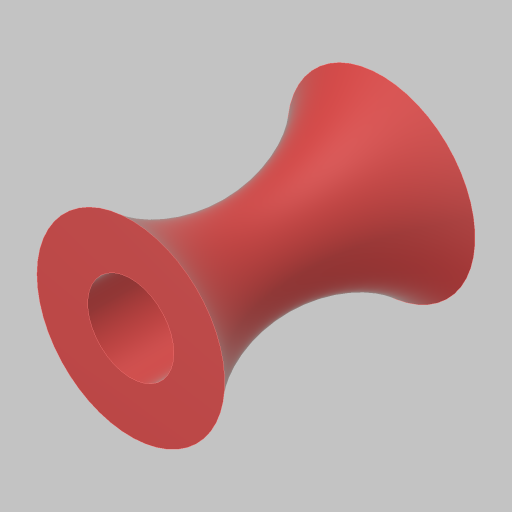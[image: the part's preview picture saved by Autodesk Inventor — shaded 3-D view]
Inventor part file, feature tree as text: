
AUTODESK INVENTOR PART (.ipt)
format: ipt  version: 2023.5 (Build 275446000, 446)  size: 182,272 bytes
history: native  units: in
note: dims shown in document units (in); Inventor stores cm internally (conversion verified against a paired STEP export)
features: sketch x2, revolve x1, extrude x1
ambient origin geometry x8: Origin, YZ Plane, XZ Plane, XY Plane, X Axis, Y Axis, Z Axis, Center Point
bodies: Solid1 (feature_tree)
feature tree (4):
  revolve  "Revolution1"  [1 undecoded]
  extrude  "Extrusion1"  TaperAngle=90.0deg  [1 undecoded]
  sketch  "Sketch1"  dims[d0=2.0in d1=0.75in]
  sketch  "Sketch2"  dims[d2=1.5in d3=90.0deg d4=0.688in d5=0.32in d6=0.0in]
note: 2 required parameter values undecoded (feature->parameter linkage not recoverable at this tier; creation-order binding heuristic only, values carry confidence <= 0.55)